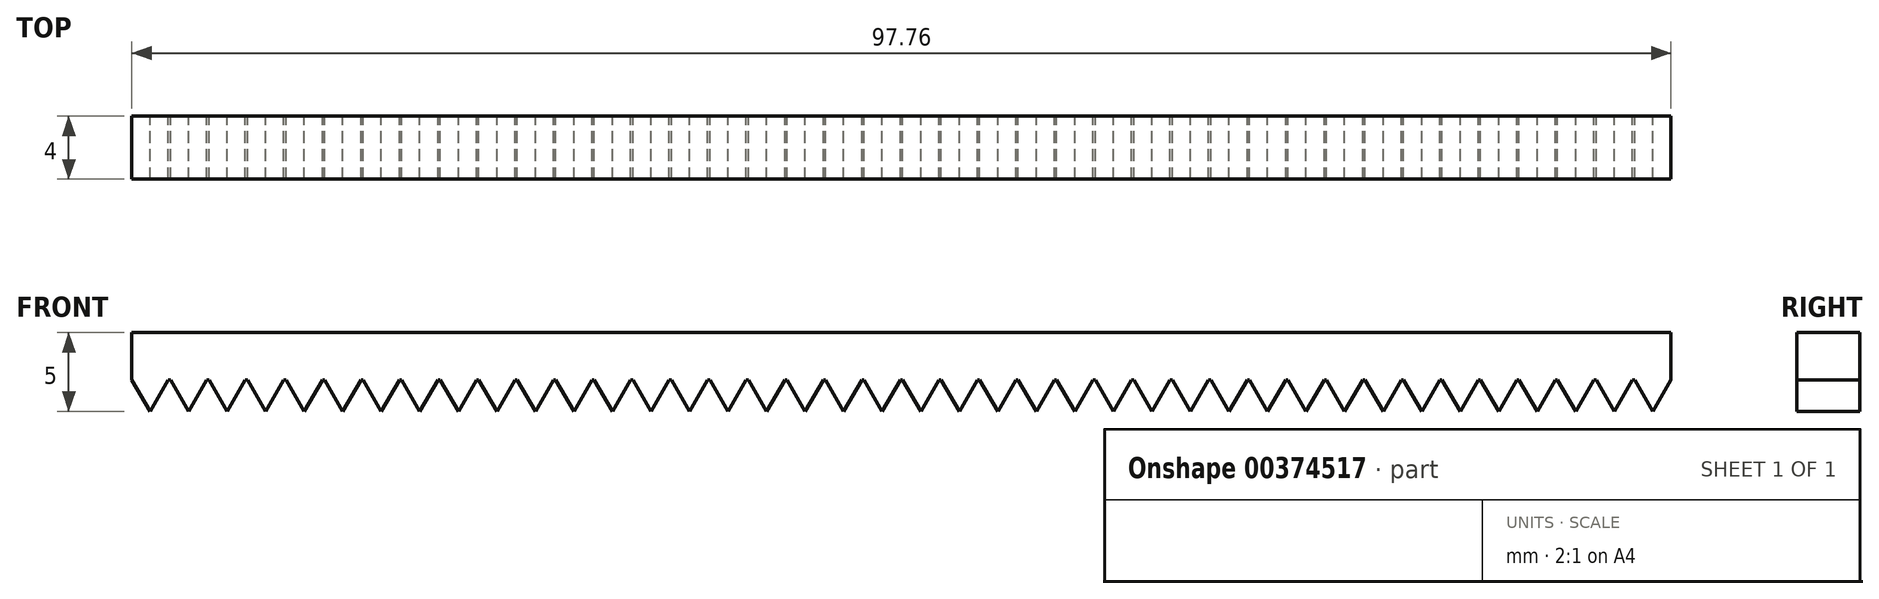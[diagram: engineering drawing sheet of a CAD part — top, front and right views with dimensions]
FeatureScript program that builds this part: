
annotation { "Feature Type Name" : "Feature", "Feature Type Description" : "" }
export const myFeature = defineFeature(function(context is Context, id is Id, definition is map)
    precondition{}
    {
        {
            var Q0;
            Q0=qCreatedBy(makeId("Front.planeOp"),FACE);
            var sketch = newSketch(context, id + "F0", { "sketchPlane" : qUnion([Q0])});
            skLineSegment(sketch, "E0.bottom", {"start": v(-48.88, 1.5) * mm, "end": v(48.88, 1.5) * mm});
            skLineSegment(sketch, "E0.top", {"start": v(-48.88, -1.5) * mm, "end": v(48.88, -1.5) * mm});
            skLineSegment(sketch, "E0.left", {"start": v(-48.88, 1.5) * mm, "end": v(-48.88, -1.5) * mm});
            skLineSegment(sketch, "E0.right", {"start": v(48.88, 1.5) * mm, "end": v(48.88, -1.5) * mm});
            skPoint(sketch, "E0.middle", {"position": v(0, 0) * mm});
            skCircle(sketch, "E1.cCircle", {"center": v(-47.72, -2.17) * mm, "radius": 0.67 * mm, "construction": true});
            skLineSegment(sketch, "E1.0", {"start": v(-48.88, -1.5) * mm, "end": v(-46.57, -1.5) * mm});
            skLineSegment(sketch, "E1.1", {"start": v(-46.57, -1.5) * mm, "end": v(-47.72, -3.5) * mm});
            skLineSegment(sketch, "E1.2", {"start": v(-47.72, -3.5) * mm, "end": v(-48.88, -1.5) * mm});
            skPoint(sketch, "E1.0.midPoint", {"position": v(-47.72, -1.5) * mm});
            skCircle(sketch, "E2.cCircle", {"center": v(-45.28, -2.17) * mm, "radius": 0.67 * mm, "construction": true});
            skLineSegment(sketch, "E2.0", {"start": v(-46.43, -1.5) * mm, "end": v(-44.12, -1.5) * mm});
            skLineSegment(sketch, "E2.1", {"start": v(-44.12, -1.5) * mm, "end": v(-45.28, -3.5) * mm});
            skLineSegment(sketch, "E2.2", {"start": v(-45.28, -3.5) * mm, "end": v(-46.43, -1.5) * mm});
            skPoint(sketch, "E2.0.midPoint", {"position": v(-45.28, -1.5) * mm});
            skCircle(sketch, "E3.cCircle", {"center": v(-42.83, -2.17) * mm, "radius": 0.67 * mm, "construction": true});
            skLineSegment(sketch, "E3.0", {"start": v(-43.98, -1.5) * mm, "end": v(-41.67, -1.5) * mm});
            skLineSegment(sketch, "E3.1", {"start": v(-41.67, -1.5) * mm, "end": v(-42.83, -3.5) * mm});
            skLineSegment(sketch, "E3.2", {"start": v(-42.83, -3.5) * mm, "end": v(-43.98, -1.5) * mm});
            skPoint(sketch, "E3.0.midPoint", {"position": v(-42.83, -1.5) * mm});
            skCircle(sketch, "E4.cCircle", {"center": v(-40.38, -2.17) * mm, "radius": 0.67 * mm, "construction": true});
            skLineSegment(sketch, "E4.0", {"start": v(-41.54, -1.5) * mm, "end": v(-39.23, -1.5) * mm});
            skLineSegment(sketch, "E4.1", {"start": v(-39.23, -1.5) * mm, "end": v(-40.38, -3.5) * mm});
            skLineSegment(sketch, "E4.2", {"start": v(-40.38, -3.5) * mm, "end": v(-41.54, -1.5) * mm});
            skPoint(sketch, "E4.0.midPoint", {"position": v(-40.38, -1.5) * mm});
            skCircle(sketch, "E5.cCircle", {"center": v(-37.93, -2.17) * mm, "radius": 0.67 * mm, "construction": true});
            skLineSegment(sketch, "E5.0", {"start": v(-39.09, -1.5) * mm, "end": v(-36.78, -1.5) * mm});
            skLineSegment(sketch, "E5.1", {"start": v(-36.78, -1.5) * mm, "end": v(-37.93, -3.5) * mm});
            skLineSegment(sketch, "E5.2", {"start": v(-37.93, -3.5) * mm, "end": v(-39.09, -1.5) * mm});
            skPoint(sketch, "E5.0.midPoint", {"position": v(-37.93, -1.5) * mm});
            skCircle(sketch, "E6.cCircle", {"center": v(-35.49, -2.17) * mm, "radius": 0.67 * mm, "construction": true});
            skLineSegment(sketch, "E6.0", {"start": v(-36.64, -1.5) * mm, "end": v(-34.33, -1.5) * mm});
            skLineSegment(sketch, "E6.1", {"start": v(-34.33, -1.5) * mm, "end": v(-35.49, -3.5) * mm});
            skLineSegment(sketch, "E6.2", {"start": v(-35.49, -3.5) * mm, "end": v(-36.64, -1.5) * mm});
            skPoint(sketch, "E6.0.midPoint", {"position": v(-35.49, -1.5) * mm});
            skCircle(sketch, "E7.cCircle", {"center": v(-33.04, -2.17) * mm, "radius": 0.67 * mm, "construction": true});
            skLineSegment(sketch, "E7.0", {"start": v(-34.2, -1.5) * mm, "end": v(-31.88, -1.5) * mm});
            skLineSegment(sketch, "E7.1", {"start": v(-31.88, -1.5) * mm, "end": v(-33.04, -3.5) * mm});
            skLineSegment(sketch, "E7.2", {"start": v(-33.04, -3.5) * mm, "end": v(-34.2, -1.5) * mm});
            skPoint(sketch, "E7.0.midPoint", {"position": v(-33.04, -1.5) * mm});
            skCircle(sketch, "E8.cCircle", {"center": v(-28.14, -2.17) * mm, "radius": 0.67 * mm, "construction": true});
            skLineSegment(sketch, "E8.0", {"start": v(-29.3, -1.5) * mm, "end": v(-27, -1.5) * mm});
            skLineSegment(sketch, "E8.1", {"start": v(-27, -1.5) * mm, "end": v(-28.14, -3.5) * mm});
            skLineSegment(sketch, "E8.2", {"start": v(-28.14, -3.5) * mm, "end": v(-29.3, -1.5) * mm});
            skPoint(sketch, "E8.0.midPoint", {"position": v(-28.14, -1.5) * mm});
            skCircle(sketch, "E9.cCircle", {"center": v(-25.7, -2.17) * mm, "radius": 0.67 * mm, "construction": true});
            skLineSegment(sketch, "E9.0", {"start": v(-26.85, -1.5) * mm, "end": v(-24.54, -1.5) * mm});
            skLineSegment(sketch, "E9.1", {"start": v(-24.54, -1.5) * mm, "end": v(-25.7, -3.5) * mm});
            skLineSegment(sketch, "E9.2", {"start": v(-25.7, -3.5) * mm, "end": v(-26.85, -1.5) * mm});
            skPoint(sketch, "E9.0.midPoint", {"position": v(-25.7, -1.5) * mm});
            skCircle(sketch, "E10.cCircle", {"center": v(-30.6, -2.17) * mm, "radius": 0.67 * mm, "construction": true});
            skLineSegment(sketch, "E10.0", {"start": v(-31.75, -1.5) * mm, "end": v(-29.44, -1.5) * mm});
            skLineSegment(sketch, "E10.1", {"start": v(-29.44, -1.5) * mm, "end": v(-30.6, -3.5) * mm});
            skLineSegment(sketch, "E10.2", {"start": v(-30.6, -3.5) * mm, "end": v(-31.75, -1.5) * mm});
            skPoint(sketch, "E10.0.midPoint", {"position": v(-30.6, -1.5) * mm});
            skCircle(sketch, "E11.cCircle", {"center": v(-23.25, -2.17) * mm, "radius": 0.67 * mm, "construction": true});
            skLineSegment(sketch, "E11.0", {"start": v(-24.4, -1.5) * mm, "end": v(-22.1, -1.5) * mm});
            skLineSegment(sketch, "E11.1", {"start": v(-22.1, -1.5) * mm, "end": v(-23.25, -3.5) * mm});
            skLineSegment(sketch, "E11.2", {"start": v(-23.25, -3.5) * mm, "end": v(-24.4, -1.5) * mm});
            skPoint(sketch, "E11.0.midPoint", {"position": v(-23.25, -1.5) * mm});
            skCircle(sketch, "E12.cCircle", {"center": v(-20.8, -2.17) * mm, "radius": 0.67 * mm, "construction": true});
            skLineSegment(sketch, "E12.0", {"start": v(-21.96, -1.5) * mm, "end": v(-19.65, -1.5) * mm});
            skLineSegment(sketch, "E12.1", {"start": v(-19.65, -1.5) * mm, "end": v(-20.8, -3.5) * mm});
            skLineSegment(sketch, "E12.2", {"start": v(-20.8, -3.5) * mm, "end": v(-21.96, -1.5) * mm});
            skPoint(sketch, "E12.0.midPoint", {"position": v(-20.8, -1.5) * mm});
            skCircle(sketch, "E13.cCircle", {"center": v(-18.36, -2.17) * mm, "radius": 0.67 * mm, "construction": true});
            skLineSegment(sketch, "E13.0", {"start": v(-19.5, -1.5) * mm, "end": v(-17.2, -1.5) * mm});
            skLineSegment(sketch, "E13.1", {"start": v(-17.2, -1.5) * mm, "end": v(-18.36, -3.5) * mm});
            skLineSegment(sketch, "E13.2", {"start": v(-18.36, -3.5) * mm, "end": v(-19.5, -1.5) * mm});
            skPoint(sketch, "E13.0.midPoint", {"position": v(-18.36, -1.5) * mm});
            skCircle(sketch, "E14.cCircle", {"center": v(-15.9, -2.17) * mm, "radius": 0.67 * mm, "construction": true});
            skLineSegment(sketch, "E14.0", {"start": v(-17.06, -1.5) * mm, "end": v(-14.75, -1.5) * mm});
            skLineSegment(sketch, "E14.1", {"start": v(-14.75, -1.5) * mm, "end": v(-15.9, -3.5) * mm});
            skLineSegment(sketch, "E14.2", {"start": v(-15.9, -3.5) * mm, "end": v(-17.06, -1.5) * mm});
            skPoint(sketch, "E14.0.midPoint", {"position": v(-15.9, -1.5) * mm});
            skCircle(sketch, "E15.cCircle", {"center": v(-13.46, -2.17) * mm, "radius": 0.67 * mm, "construction": true});
            skLineSegment(sketch, "E15.0", {"start": v(-14.62, -1.5) * mm, "end": v(-12.3, -1.5) * mm});
            skLineSegment(sketch, "E15.1", {"start": v(-12.3, -1.5) * mm, "end": v(-13.46, -3.5) * mm});
            skLineSegment(sketch, "E15.2", {"start": v(-13.46, -3.5) * mm, "end": v(-14.62, -1.5) * mm});
            skPoint(sketch, "E15.0.midPoint", {"position": v(-13.46, -1.5) * mm});
            skCircle(sketch, "E16.cCircle", {"center": v(-11.01, -2.17) * mm, "radius": 0.67 * mm, "construction": true});
            skLineSegment(sketch, "E16.0", {"start": v(-12.17, -1.5) * mm, "end": v(-9.86, -1.5) * mm});
            skLineSegment(sketch, "E16.1", {"start": v(-9.86, -1.5) * mm, "end": v(-11.01, -3.5) * mm});
            skLineSegment(sketch, "E16.2", {"start": v(-11.01, -3.5) * mm, "end": v(-12.17, -1.5) * mm});
            skPoint(sketch, "E16.0.midPoint", {"position": v(-11.01, -1.5) * mm});
            skCircle(sketch, "E17.cCircle", {"center": v(-8.57, -2.17) * mm, "radius": 0.67 * mm, "construction": true});
            skLineSegment(sketch, "E17.0", {"start": v(-9.72, -1.5) * mm, "end": v(-7.41, -1.5) * mm});
            skLineSegment(sketch, "E17.1", {"start": v(-7.41, -1.5) * mm, "end": v(-8.57, -3.5) * mm});
            skLineSegment(sketch, "E17.2", {"start": v(-8.57, -3.5) * mm, "end": v(-9.72, -1.5) * mm});
            skPoint(sketch, "E17.0.midPoint", {"position": v(-8.57, -1.5) * mm});
            skCircle(sketch, "E18.cCircle", {"center": v(-6.12, -2.17) * mm, "radius": 0.67 * mm, "construction": true});
            skLineSegment(sketch, "E18.0", {"start": v(-7.27, -1.5) * mm, "end": v(-4.96, -1.5) * mm});
            skLineSegment(sketch, "E18.1", {"start": v(-4.96, -1.5) * mm, "end": v(-6.12, -3.5) * mm});
            skLineSegment(sketch, "E18.2", {"start": v(-6.12, -3.5) * mm, "end": v(-7.27, -1.5) * mm});
            skPoint(sketch, "E18.0.midPoint", {"position": v(-6.12, -1.5) * mm});
            skCircle(sketch, "E19.cCircle", {"center": v(-3.67, -2.17) * mm, "radius": 0.67 * mm, "construction": true});
            skLineSegment(sketch, "E19.0", {"start": v(-4.83, -1.5) * mm, "end": v(-2.52, -1.5) * mm});
            skLineSegment(sketch, "E19.1", {"start": v(-2.52, -1.5) * mm, "end": v(-3.67, -3.5) * mm});
            skLineSegment(sketch, "E19.2", {"start": v(-3.67, -3.5) * mm, "end": v(-4.83, -1.5) * mm});
            skPoint(sketch, "E19.0.midPoint", {"position": v(-3.67, -1.5) * mm});
            skCircle(sketch, "E20.cCircle", {"center": v(-1.22, -2.17) * mm, "radius": 0.67 * mm, "construction": true});
            skLineSegment(sketch, "E20.0", {"start": v(-2.38, -1.5) * mm, "end": v(-0.07, -1.5) * mm});
            skLineSegment(sketch, "E20.1", {"start": v(-0.07, -1.5) * mm, "end": v(-1.22, -3.5) * mm});
            skLineSegment(sketch, "E20.2", {"start": v(-1.22, -3.5) * mm, "end": v(-2.38, -1.5) * mm});
            skPoint(sketch, "E20.0.midPoint", {"position": v(-1.22, -1.5) * mm});
            skCircle(sketch, "E21.cCircle", {"center": v(1.22, -2.17) * mm, "radius": 0.67 * mm, "construction": true});
            skLineSegment(sketch, "E21.0", {"start": v(0.07, -1.5) * mm, "end": v(2.38, -1.5) * mm});
            skLineSegment(sketch, "E21.1", {"start": v(2.38, -1.5) * mm, "end": v(1.22, -3.5) * mm});
            skLineSegment(sketch, "E21.2", {"start": v(1.22, -3.5) * mm, "end": v(0.07, -1.5) * mm});
            skPoint(sketch, "E21.0.midPoint", {"position": v(1.22, -1.5) * mm});
            skCircle(sketch, "E22.cCircle", {"center": v(3.67, -2.17) * mm, "radius": 0.67 * mm, "construction": true});
            skLineSegment(sketch, "E22.0", {"start": v(2.52, -1.5) * mm, "end": v(4.83, -1.5) * mm});
            skLineSegment(sketch, "E22.1", {"start": v(4.83, -1.5) * mm, "end": v(3.67, -3.5) * mm});
            skLineSegment(sketch, "E22.2", {"start": v(3.67, -3.5) * mm, "end": v(2.52, -1.5) * mm});
            skPoint(sketch, "E22.0.midPoint", {"position": v(3.67, -1.5) * mm});
            skCircle(sketch, "E23.cCircle", {"center": v(8.57, -2.17) * mm, "radius": 0.67 * mm, "construction": true});
            skLineSegment(sketch, "E23.0", {"start": v(7.41, -1.5) * mm, "end": v(9.72, -1.5) * mm});
            skLineSegment(sketch, "E23.1", {"start": v(9.72, -1.5) * mm, "end": v(8.57, -3.5) * mm});
            skLineSegment(sketch, "E23.2", {"start": v(8.57, -3.5) * mm, "end": v(7.41, -1.5) * mm});
            skPoint(sketch, "E23.0.midPoint", {"position": v(8.57, -1.5) * mm});
            skCircle(sketch, "E24.cCircle", {"center": v(6.12, -2.17) * mm, "radius": 0.67 * mm, "construction": true});
            skLineSegment(sketch, "E24.0", {"start": v(4.96, -1.5) * mm, "end": v(7.27, -1.5) * mm});
            skLineSegment(sketch, "E24.1", {"start": v(7.27, -1.5) * mm, "end": v(6.12, -3.5) * mm});
            skLineSegment(sketch, "E24.2", {"start": v(6.12, -3.5) * mm, "end": v(4.96, -1.5) * mm});
            skPoint(sketch, "E24.0.midPoint", {"position": v(6.12, -1.5) * mm});
            skCircle(sketch, "E25.cCircle", {"center": v(13.46, -2.17) * mm, "radius": 0.67 * mm, "construction": true});
            skLineSegment(sketch, "E25.0", {"start": v(12.3, -1.5) * mm, "end": v(14.62, -1.5) * mm});
            skLineSegment(sketch, "E25.1", {"start": v(14.62, -1.5) * mm, "end": v(13.46, -3.5) * mm});
            skLineSegment(sketch, "E25.2", {"start": v(13.46, -3.5) * mm, "end": v(12.3, -1.5) * mm});
            skPoint(sketch, "E25.0.midPoint", {"position": v(13.46, -1.5) * mm});
            skCircle(sketch, "E26.cCircle", {"center": v(11.01, -2.17) * mm, "radius": 0.67 * mm, "construction": true});
            skLineSegment(sketch, "E26.0", {"start": v(9.86, -1.5) * mm, "end": v(12.17, -1.5) * mm});
            skLineSegment(sketch, "E26.1", {"start": v(12.17, -1.5) * mm, "end": v(11.01, -3.5) * mm});
            skLineSegment(sketch, "E26.2", {"start": v(11.01, -3.5) * mm, "end": v(9.86, -1.5) * mm});
            skPoint(sketch, "E26.0.midPoint", {"position": v(11.01, -1.5) * mm});
            skCircle(sketch, "E27.cCircle", {"center": v(15.9, -2.17) * mm, "radius": 0.67 * mm, "construction": true});
            skLineSegment(sketch, "E27.0", {"start": v(14.75, -1.5) * mm, "end": v(17.06, -1.5) * mm});
            skLineSegment(sketch, "E27.1", {"start": v(17.06, -1.5) * mm, "end": v(15.9, -3.5) * mm});
            skLineSegment(sketch, "E27.2", {"start": v(15.9, -3.5) * mm, "end": v(14.75, -1.5) * mm});
            skPoint(sketch, "E27.0.midPoint", {"position": v(15.9, -1.5) * mm});
            skCircle(sketch, "E28.cCircle", {"center": v(18.36, -2.17) * mm, "radius": 0.67 * mm, "construction": true});
            skLineSegment(sketch, "E28.0", {"start": v(17.2, -1.5) * mm, "end": v(19.5, -1.5) * mm});
            skLineSegment(sketch, "E28.1", {"start": v(19.5, -1.5) * mm, "end": v(18.36, -3.5) * mm});
            skLineSegment(sketch, "E28.2", {"start": v(18.36, -3.5) * mm, "end": v(17.2, -1.5) * mm});
            skPoint(sketch, "E28.0.midPoint", {"position": v(18.36, -1.5) * mm});
            skLineSegment(sketch, "E29.0", {"start": v(21.56, -1.5) * mm, "end": v(23.87, -1.5) * mm});
            skPoint(sketch, "E29.0.midPoint", {"position": v(22.72, -1.5) * mm});
            skCircle(sketch, "E30.cCircle", {"center": v(20.8, -2.17) * mm, "radius": 0.67 * mm, "construction": true});
            skLineSegment(sketch, "E30.0", {"start": v(19.65, -1.5) * mm, "end": v(21.96, -1.5) * mm});
            skLineSegment(sketch, "E30.1", {"start": v(21.96, -1.5) * mm, "end": v(20.8, -3.5) * mm});
            skLineSegment(sketch, "E30.2", {"start": v(20.8, -3.5) * mm, "end": v(19.65, -1.5) * mm});
            skPoint(sketch, "E30.0.midPoint", {"position": v(20.8, -1.5) * mm});
            skCircle(sketch, "E31.cCircle", {"center": v(25.7, -2.17) * mm, "radius": 0.67 * mm, "construction": true});
            skLineSegment(sketch, "E31.0", {"start": v(24.54, -1.5) * mm, "end": v(26.85, -1.5) * mm});
            skLineSegment(sketch, "E31.1", {"start": v(26.85, -1.5) * mm, "end": v(25.7, -3.5) * mm});
            skLineSegment(sketch, "E31.2", {"start": v(25.7, -3.5) * mm, "end": v(24.54, -1.5) * mm});
            skPoint(sketch, "E31.0.midPoint", {"position": v(25.7, -1.5) * mm});
            skCircle(sketch, "E32.cCircle", {"center": v(23.25, -2.17) * mm, "radius": 0.67 * mm, "construction": true});
            skLineSegment(sketch, "E32.0", {"start": v(22.1, -1.5) * mm, "end": v(24.4, -1.5) * mm});
            skLineSegment(sketch, "E32.1", {"start": v(24.4, -1.5) * mm, "end": v(23.25, -3.5) * mm});
            skLineSegment(sketch, "E32.2", {"start": v(23.25, -3.5) * mm, "end": v(22.1, -1.5) * mm});
            skPoint(sketch, "E32.0.midPoint", {"position": v(23.25, -1.5) * mm});
            skCircle(sketch, "E33.cCircle", {"center": v(30.6, -2.17) * mm, "radius": 0.67 * mm, "construction": true});
            skLineSegment(sketch, "E33.0", {"start": v(29.44, -1.5) * mm, "end": v(31.75, -1.5) * mm});
            skLineSegment(sketch, "E33.1", {"start": v(31.75, -1.5) * mm, "end": v(30.6, -3.5) * mm});
            skLineSegment(sketch, "E33.2", {"start": v(30.6, -3.5) * mm, "end": v(29.44, -1.5) * mm});
            skPoint(sketch, "E33.0.midPoint", {"position": v(30.6, -1.5) * mm});
            skCircle(sketch, "E34.cCircle", {"center": v(33.04, -2.17) * mm, "radius": 0.67 * mm, "construction": true});
            skLineSegment(sketch, "E34.0", {"start": v(31.88, -1.5) * mm, "end": v(34.2, -1.5) * mm});
            skLineSegment(sketch, "E34.1", {"start": v(34.2, -1.5) * mm, "end": v(33.04, -3.5) * mm});
            skLineSegment(sketch, "E34.2", {"start": v(33.04, -3.5) * mm, "end": v(31.88, -1.5) * mm});
            skPoint(sketch, "E34.0.midPoint", {"position": v(33.04, -1.5) * mm});
            skCircle(sketch, "E35.cCircle", {"center": v(28.14, -2.17) * mm, "radius": 0.67 * mm, "construction": true});
            skLineSegment(sketch, "E35.0", {"start": v(27, -1.5) * mm, "end": v(29.3, -1.5) * mm});
            skLineSegment(sketch, "E35.1", {"start": v(29.3, -1.5) * mm, "end": v(28.14, -3.5) * mm});
            skLineSegment(sketch, "E35.2", {"start": v(28.14, -3.5) * mm, "end": v(27, -1.5) * mm});
            skPoint(sketch, "E35.0.midPoint", {"position": v(28.14, -1.5) * mm});
            skCircle(sketch, "E36.cCircle", {"center": v(35.49, -2.17) * mm, "radius": 0.67 * mm, "construction": true});
            skLineSegment(sketch, "E36.0", {"start": v(34.33, -1.5) * mm, "end": v(36.64, -1.5) * mm});
            skLineSegment(sketch, "E36.1", {"start": v(36.64, -1.5) * mm, "end": v(35.49, -3.5) * mm});
            skLineSegment(sketch, "E36.2", {"start": v(35.49, -3.5) * mm, "end": v(34.33, -1.5) * mm});
            skPoint(sketch, "E36.0.midPoint", {"position": v(35.49, -1.5) * mm});
            skCircle(sketch, "E37.cCircle", {"center": v(37.93, -2.17) * mm, "radius": 0.67 * mm, "construction": true});
            skLineSegment(sketch, "E37.0", {"start": v(36.78, -1.5) * mm, "end": v(39.09, -1.5) * mm});
            skLineSegment(sketch, "E37.1", {"start": v(39.09, -1.5) * mm, "end": v(37.93, -3.5) * mm});
            skLineSegment(sketch, "E37.2", {"start": v(37.93, -3.5) * mm, "end": v(36.78, -1.5) * mm});
            skPoint(sketch, "E37.0.midPoint", {"position": v(37.93, -1.5) * mm});
            skCircle(sketch, "E38.cCircle", {"center": v(42.83, -2.17) * mm, "radius": 0.67 * mm, "construction": true});
            skLineSegment(sketch, "E38.0", {"start": v(41.67, -1.5) * mm, "end": v(43.98, -1.5) * mm});
            skLineSegment(sketch, "E38.1", {"start": v(43.98, -1.5) * mm, "end": v(42.83, -3.5) * mm});
            skLineSegment(sketch, "E38.2", {"start": v(42.83, -3.5) * mm, "end": v(41.67, -1.5) * mm});
            skPoint(sketch, "E38.0.midPoint", {"position": v(42.83, -1.5) * mm});
            skCircle(sketch, "E39.cCircle", {"center": v(45.28, -2.17) * mm, "radius": 0.67 * mm, "construction": true});
            skLineSegment(sketch, "E39.0", {"start": v(44.12, -1.5) * mm, "end": v(46.43, -1.5) * mm});
            skLineSegment(sketch, "E39.1", {"start": v(46.43, -1.5) * mm, "end": v(45.28, -3.5) * mm});
            skLineSegment(sketch, "E39.2", {"start": v(45.28, -3.5) * mm, "end": v(44.12, -1.5) * mm});
            skPoint(sketch, "E39.0.midPoint", {"position": v(45.28, -1.5) * mm});
            skCircle(sketch, "E40.cCircle", {"center": v(40.38, -2.17) * mm, "radius": 0.67 * mm, "construction": true});
            skLineSegment(sketch, "E40.0", {"start": v(39.23, -1.5) * mm, "end": v(41.54, -1.5) * mm});
            skLineSegment(sketch, "E40.1", {"start": v(41.54, -1.5) * mm, "end": v(40.38, -3.5) * mm});
            skLineSegment(sketch, "E40.2", {"start": v(40.38, -3.5) * mm, "end": v(39.23, -1.5) * mm});
            skPoint(sketch, "E40.0.midPoint", {"position": v(40.38, -1.5) * mm});
            skCircle(sketch, "E41.cCircle", {"center": v(47.72, -2.17) * mm, "radius": 0.67 * mm, "construction": true});
            skLineSegment(sketch, "E41.0", {"start": v(46.57, -1.5) * mm, "end": v(48.88, -1.5) * mm});
            skLineSegment(sketch, "E41.1", {"start": v(48.88, -1.5) * mm, "end": v(47.72, -3.5) * mm});
            skLineSegment(sketch, "E41.2", {"start": v(47.72, -3.5) * mm, "end": v(46.57, -1.5) * mm});
            skPoint(sketch, "E41.0.midPoint", {"position": v(47.72, -1.5) * mm});
            skSolve(sketch);
        }
        {
            var Q0;
            Q0 = qSketchRegion(id + "F0", true);
            extrude(context, id + "F1", {"entities" : qUnion([Q0]), "depth" : 4 * mm});
        }
    });
